# Revit family: Domotics-DomesticRanges-GEWISS-CHORUS_CONTAINER_INSTRUMENT_WHITE
name_source: partatom
category: Apparecchi elettrici
revit_build: Autodesk Revit 2016 (Build: 20161004_0715(x64)
units: mm (PartAtom-declared; Revit-internal decimal feet)

## family parameters
Basato su piano di lavoro = No
Condiviso = No
Mantenere orientamento annotazione = No
Punto di calcolo locali = Sì
Quota connettore circolare = Usa diametro
Sempre verticale = Sì
Taglio con vuoti quando caricato = No
Tipo di parte = Normale

## types (2) — shared parameters
Catalogue = DOMOTICS
Catalogue Range = CHORUS - DOMESTIC RANGE
Colour = White
Electrocod = 0122
Glow Wire Test = 650 °C
Glow wire test: = 650 °C
IDF = 7f89638b-f7e1-453d-9a1f-0e100603e236
IDT = ac57cf95-720a-4d37-b923-c4ffb006943d
Immagine tipo = GW16854.jpg
Larghezza = 181 mm  [stored 0.593832 ft]
Material = Rectangular
Materiale_ = GEWISS BIANCO
Produttore = GEWISS S.p.A.
SEO = Panel
Standard = EN 60670-1
Standard; = EN 60670-1
Suitable for plates = ONE
Technical sheet = https://www.gewiss.com
Thermo-pressure with ball = 70
Torque screws tightening = 0,8NM
URL = https://www.gewiss.com
Version file RFA = 18.0

## per-type parameters (varying)
| type | Description: | Descrizione | EAN code | Modello | Outer dim. LxHxD (mm) | Support |
| GW16854 - Table plate 4P White | 4 gang | TABLE AND WALL PLATE, 4-GANG, WHITE | 8011564279421 | GW16854 | 140x90x69 | GW16804 |
| GW16856 - Table plate 6P White | 6 gang | TABLE AND WALL PLATE, 6-GANG, WHITE | 8011564279438 | GW16856 | 181x90x69 | GW16806 |

note: source unit labels omitted for Thermo-pressure with ball — the stored unit's dimension contradicts the parameter name (converter mislabeling)

note: [stored X ft] marks values corroborated as IEEE doubles in the binary element streams (Revit-internal decimal feet)
